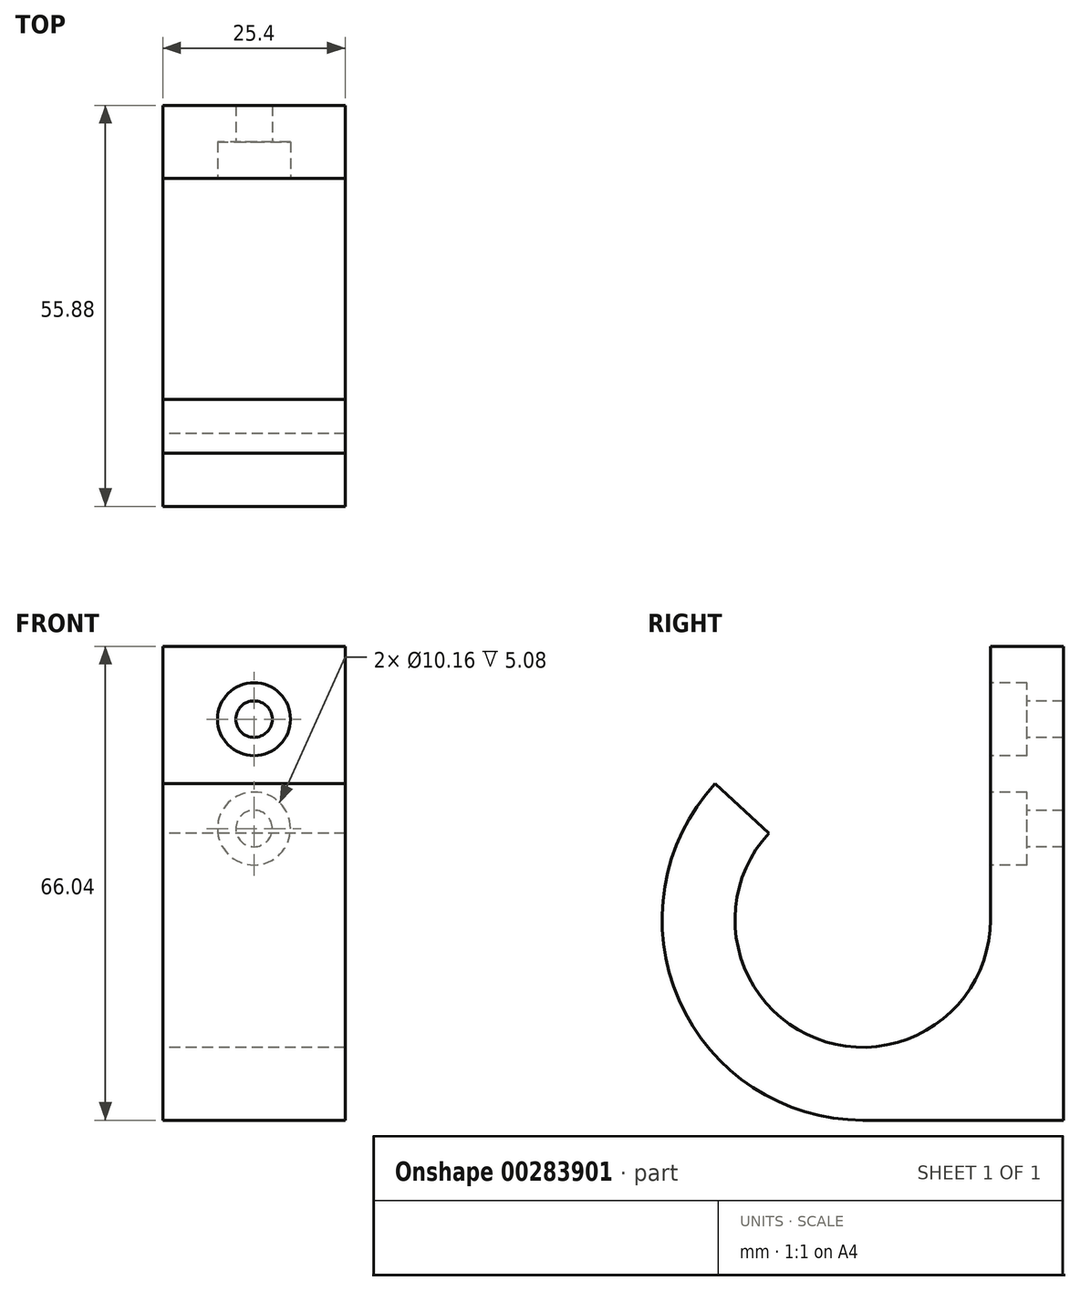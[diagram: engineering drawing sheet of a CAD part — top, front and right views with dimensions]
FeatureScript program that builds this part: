
annotation { "Feature Type Name" : "Feature", "Feature Type Description" : "" }
export const myFeature = defineFeature(function(context is Context, id is Id, definition is map)
    precondition{}
    {
        {
            var Q0;
            Q0=qCreatedBy(makeId("Right.planeOp"),FACE);
            var sketch = newSketch(context, id + "F0", { "sketchPlane" : qUnion([Q0])});
            skLineSegment(sketch, "E0", {"start": v(0, 0) * mm, "end": v(0, 38.1) * mm});
            skArc(sketch, "E1", {"start": v(0, 0) * mm, "mid": v(-17.78, -17.78) * mm, "end": v(-35.56, 0) * mm});
            skArc(sketch, "E2", {"start": v(-35.56, 0) * mm, "mid": v(-34.34, 6.47) * mm, "end": v(-30.85, 12.05) * mm});
            skArc(sketch, "E3.0", {"start": v(-45.72, 0) * mm, "mid": v(-43.8, 10.17) * mm, "end": v(-38.32, 18.94) * mm});
            skArc(sketch, "E3.1", {"start": v(10.16, 0) * mm, "mid": v(-17.78, -27.94) * mm, "end": v(-45.72, 0) * mm});
            skLineSegment(sketch, "E3.2", {"start": v(10.16, 0) * mm, "end": v(10.16, 38.1) * mm});
            skLineSegment(sketch, "E4", {"start": v(-17.78, 0) * mm, "end": v(-17.78, -27.94) * mm, "construction": true});
            skLineSegment(sketch, "E5", {"start": v(10.16, 0) * mm, "end": v(10.16, -27.94) * mm});
            skLineSegment(sketch, "E6", {"start": v(10.16, -27.94) * mm, "end": v(-17.78, -27.94) * mm});
            skLineSegment(sketch, "E7", {"start": v(-38.32, 18.94) * mm, "end": v(-30.85, 12.05) * mm});
            skLineSegment(sketch, "E8", {"start": v(0, 38.1) * mm, "end": v(10.16, 38.1) * mm});
            skSolve(sketch);
        }
        {
            var Q0;
            Q0=qSketchRegion(id+"F0",true);
            extrude(context, id + "F1", {"entities" : qUnion([Q0]), "endBound" : BoundingType.SYMMETRIC, "depth" : 25.4 * mm});
        }
        {
            var Q0;
            Q0=makeQuery(id+"F1.opExtrude","SWEPT_FACE",FACE,{"disambiguationData":[OSD([sQuery(id+"F0.wireOp",EDGE,"E0")])]});
            var sketch = newSketch(context, id + "F2", { "sketchPlane" : qUnion([Q0])});
            skLineSegment(sketch, "E9", {"start": v(0, 0) * mm, "end": v(0, 12.7) * mm, "construction": true});
            skCircle(sketch, "E10", {"center": v(0, 12.7) * mm, "radius": 2.54 * mm});
            skCircle(sketch, "E11", {"center": v(0, 27.94) * mm, "radius": 2.54 * mm});
            skCircle(sketch, "E12.0", {"center": v(0, 27.94) * mm, "radius": 5.08 * mm});
            skCircle(sketch, "E13.0", {"center": v(0, 12.7) * mm, "radius": 5.08 * mm});
            skSolve(sketch);
        }
        {
            var Q0;
            Q0=makeQuery(id+"F2.imprint","IMPRINT",FACE,{"disambiguationData":[TD([[makeQuery(id+"F2.imprint","IMPRINT",EDGE,{"derivedFrom":sQuery(id+"F2.wireOp",EDGE,"E11")}),1.0]])]});
            var Q1;
            Q1=makeQuery(id+"F2.imprint","IMPRINT",FACE,{"disambiguationData":[TD([[makeQuery(id+"F2.imprint","IMPRINT",EDGE,{"derivedFrom":sQuery(id+"F2.wireOp",EDGE,"E10")}),1.0]])]});
            extrude(context, id + "F3", {"entities" : qUnion([Q0, Q1]), "operationType" : NewBodyOperationType.REMOVE, "endBound" : BoundingType.THROUGH_ALL, "oppositeDirection" : true, "depth" : 25.4 * mm});
        }
        {
            var Q0;
            Q0=qSketchRegion(id+"F2",true);
            extrude(context, id + "F4", {"entities" : qUnion([Q0]), "operationType" : NewBodyOperationType.REMOVE, "oppositeDirection" : true, "depth" : 5.08 * mm});
        }
    });
